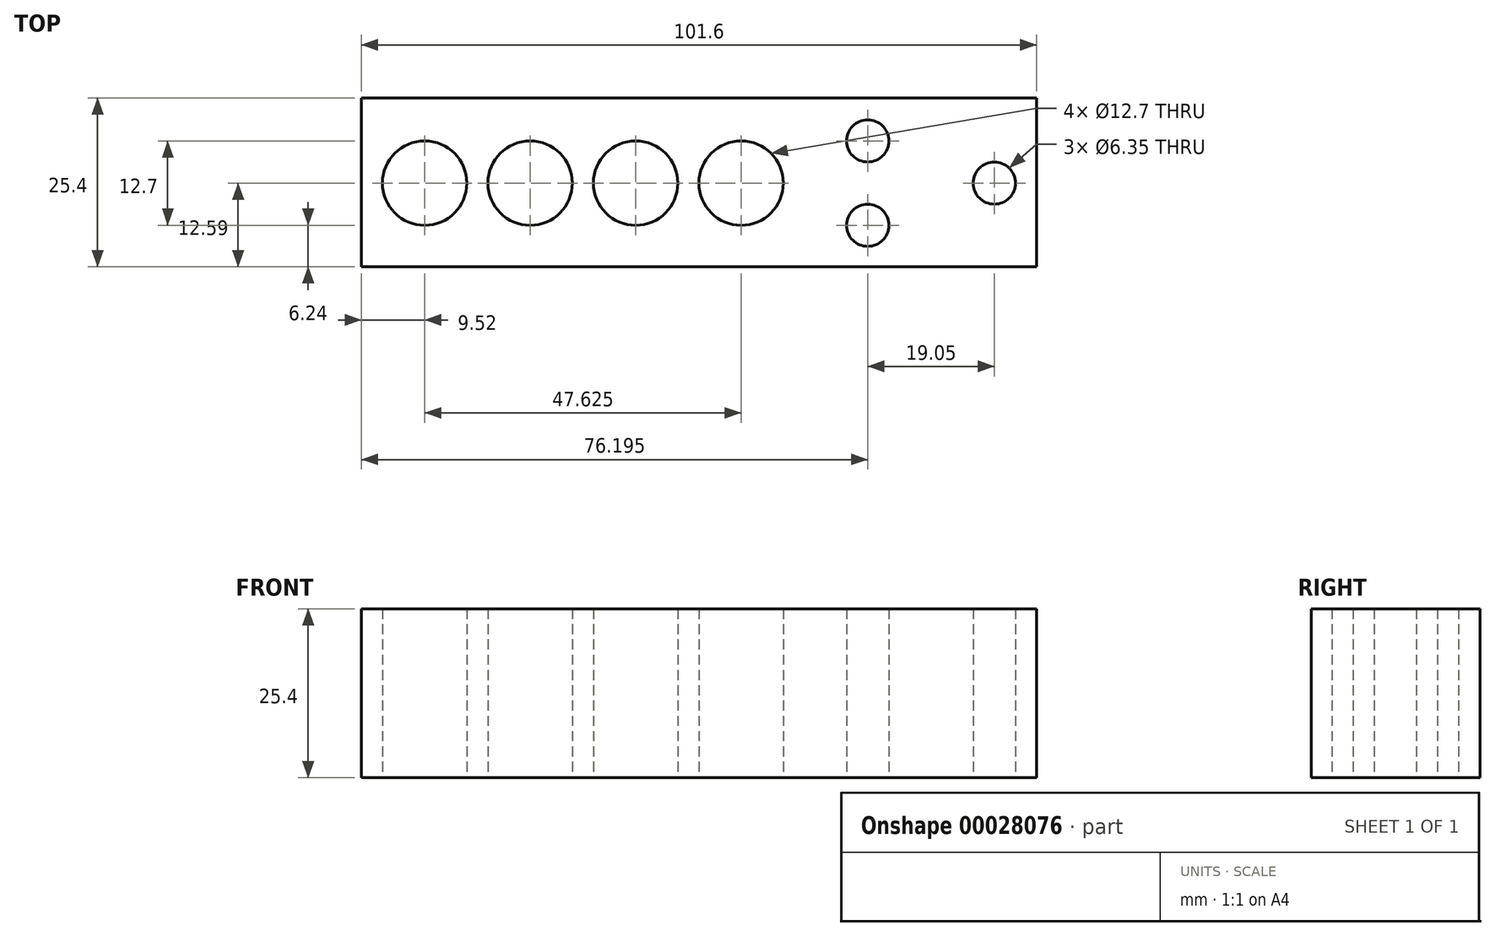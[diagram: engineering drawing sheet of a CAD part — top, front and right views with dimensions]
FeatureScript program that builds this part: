
annotation { "Feature Type Name" : "Feature", "Feature Type Description" : "" }
export const myFeature = defineFeature(function(context is Context, id is Id, definition is map)
    precondition{}
    {
        {
            var Q0;
            Q0=qCreatedBy(makeId("Top.planeOp"),FACE);
            var sketch = newSketch(context, id + "F0", { "sketchPlane" : qUnion([Q0])});
            skLineSegment(sketch, "E0.bottom", {"start": v(-41.07, 12.81) * mm, "end": v(60.53, 12.81) * mm});
            skLineSegment(sketch, "E0.top", {"start": v(-41.07, -12.59) * mm, "end": v(60.53, -12.59) * mm});
            skLineSegment(sketch, "E0.left", {"start": v(-41.07, 12.81) * mm, "end": v(-41.07, -12.59) * mm});
            skLineSegment(sketch, "E0.right", {"start": v(60.53, 12.81) * mm, "end": v(60.53, -12.59) * mm});
            skCircle(sketch, "E1", {"center": v(-31.55, 0) * mm, "radius": 6.35 * mm});
            skCircle(sketch, "E2", {"center": v(-15.67, 0) * mm, "radius": 6.35 * mm});
            skCircle(sketch, "E3", {"center": v(0.2, 0) * mm, "radius": 6.35 * mm});
            skCircle(sketch, "E4", {"center": v(16.08, 0) * mm, "radius": 6.35 * mm});
            skCircle(sketch, "E5", {"center": v(35.13, 6.35) * mm, "radius": 3.18 * mm});
            skCircle(sketch, "E6", {"center": v(35.13, -6.35) * mm, "radius": 3.18 * mm});
            skCircle(sketch, "E7", {"center": v(54.18, 0) * mm, "radius": 3.18 * mm});
            skSolve(sketch);
        }
        {
            var Q0;
            Q0=makeQuery(id+"F0.imprint","IMPRINT",FACE,{"disambiguationData":[TD([[makeQuery(id+"F0.imprint","IMPRINT",EDGE,{"derivedFrom":sQuery(id+"F0.wireOp",EDGE,"E0.bottom")}),-1.0]])]});
            extrude(context, id + "F1", {"entities" : qUnion([Q0]), "depth" : 25.4 * mm});
        }
    });
